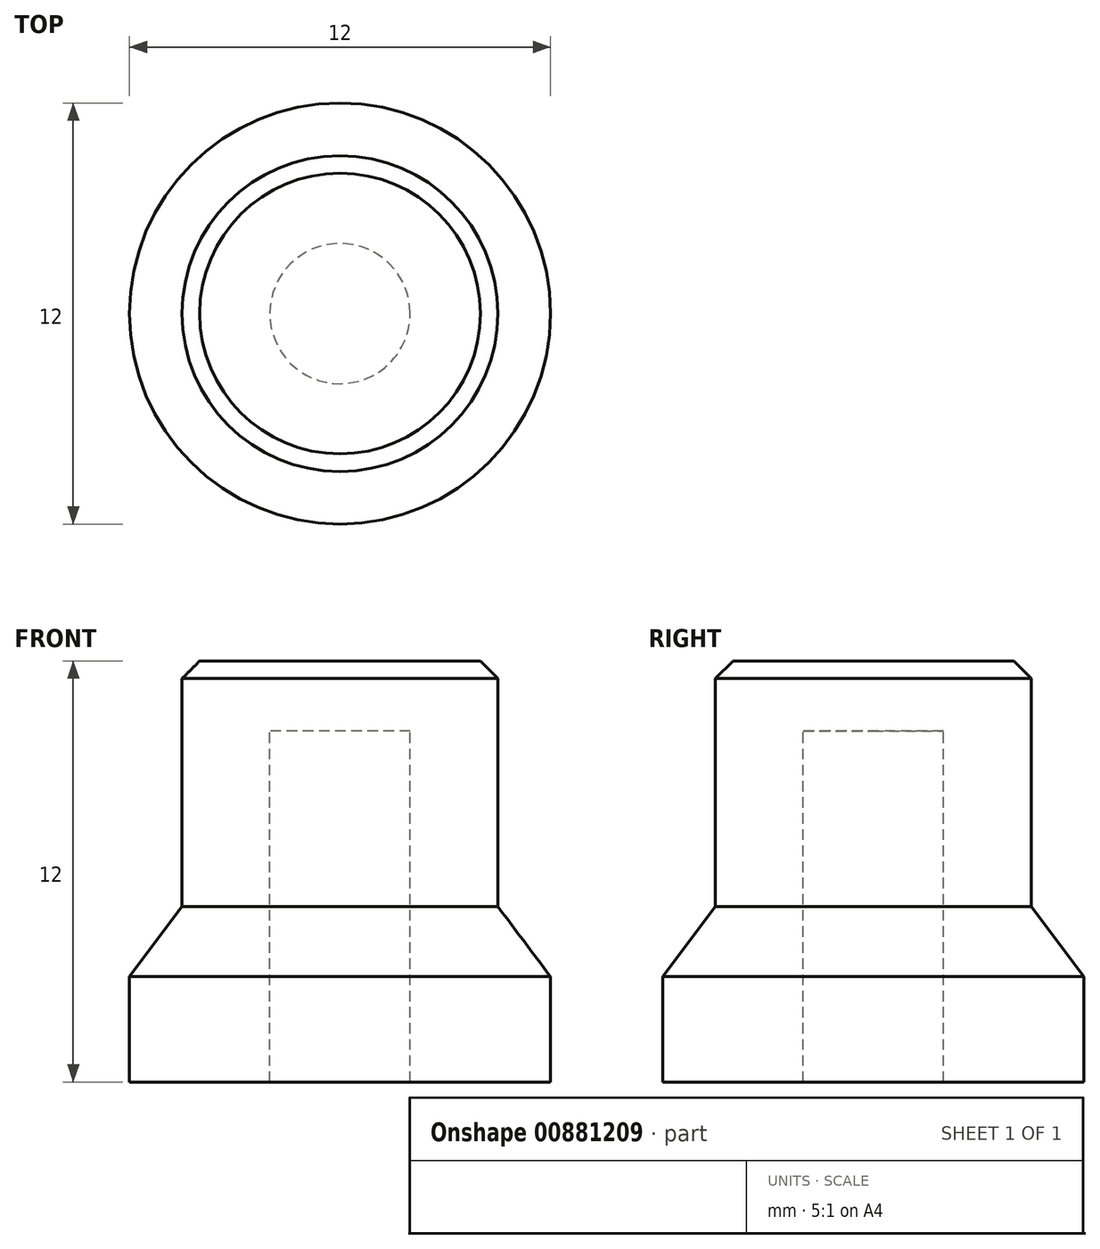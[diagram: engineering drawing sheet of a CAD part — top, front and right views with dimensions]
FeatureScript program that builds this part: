
annotation { "Feature Type Name" : "Feature", "Feature Type Description" : "" }
export const myFeature = defineFeature(function(context is Context, id is Id, definition is map)
    precondition{}
    {
        {
            var Q0;
            Q0=qCreatedBy(makeId("Front.planeOp"),FACE);
            var sketch = newSketch(context, id + "F0", { "sketchPlane" : qUnion([Q0])});
            skLineSegment(sketch, "E0", {"start": v(-2, 0.5) * mm, "end": v(-6, 0.5) * mm});
            skLineSegment(sketch, "E1", {"start": v(-6, 0.5) * mm, "end": v(-6, 3.5) * mm});
            skLineSegment(sketch, "E2", {"start": v(-6, 3.5) * mm, "end": v(-4.5, 5.5) * mm});
            skLineSegment(sketch, "E3", {"start": v(-4.5, 5.5) * mm, "end": v(-4.5, 12.5) * mm});
            skLineSegment(sketch, "E4", {"start": v(-4.5, 12.5) * mm, "end": v(0, 12.5) * mm});
            skLineSegment(sketch, "E5", {"start": v(0, 12.5) * mm, "end": v(0, 10.5) * mm});
            skLineSegment(sketch, "E6", {"start": v(-2, 0.5) * mm, "end": v(-2, 10.5) * mm});
            skLineSegment(sketch, "E7", {"start": v(-2, 10.5) * mm, "end": v(0, 10.5) * mm});
            skSolve(sketch);
        }
        {
            var Q0;
            Q0=makeQuery(id+"F0.imprint","IMPRINT",FACE,{"disambiguationData":[TD([[makeQuery(id+"F0.imprint","IMPRINT",EDGE,{"derivedFrom":sQuery(id+"F0.wireOp",EDGE,"E0")}),-1.0]])]});
            var Q1;
            Q1=sQuery(id+"F0.wireOp",EDGE,"E5");
            revolve(context, id + "F1", {"surfaceOperationType" : NewSurfaceOperationType.NEW, "entities" : qUnion([Q0]), "axis" : qUnion([Q1]), "revolveType" : RevolveType.FULL});
        }
        {
            var Q0;
            Q0=makeQuery(id+"F1.opRevolve","SWEPT_FACE",FACE,{"disambiguationData":[OSD([sQuery(id+"F0.wireOp",EDGE,"E4")])]});
            chamfer(context, id + "F2", {"entities" : qUnion([Q0]), "width" : 0.5 * mm, "tangentPropagation" : true});
        }
    });
